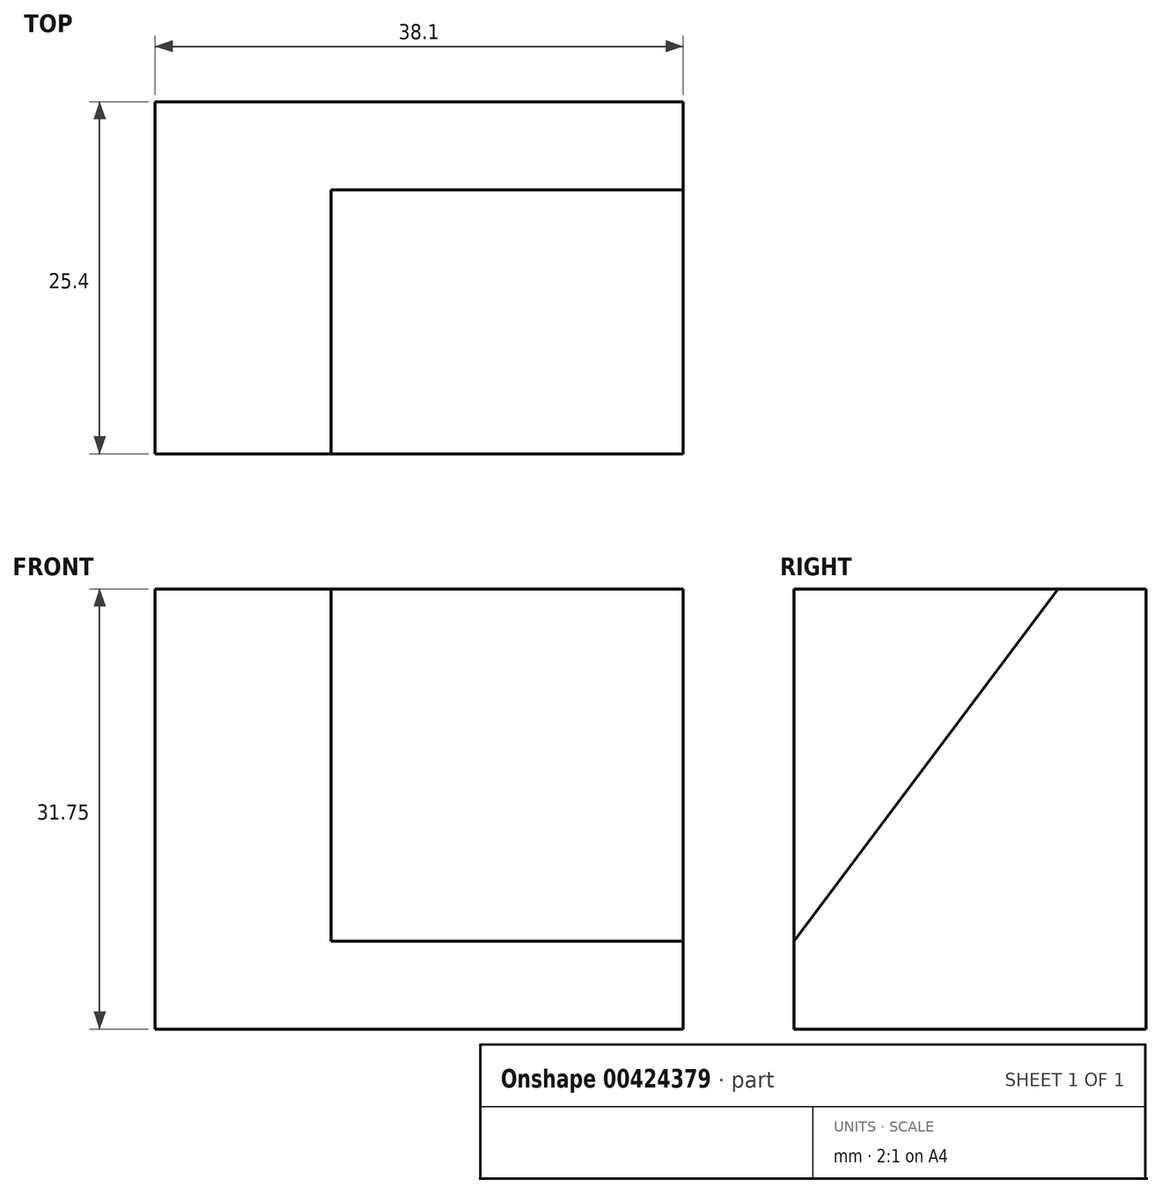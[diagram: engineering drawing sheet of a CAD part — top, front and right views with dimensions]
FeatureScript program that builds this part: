
annotation { "Feature Type Name" : "Feature", "Feature Type Description" : "" }
export const myFeature = defineFeature(function(context is Context, id is Id, definition is map)
    precondition{}
    {
        {
            var Q0;
            Q0=qCreatedBy(makeId("Top.planeOp"),FACE);
            var sketch = newSketch(context, id + "F0", { "sketchPlane" : qUnion([Q0])});
            skLineSegment(sketch, "E0", {"start": v(0, 0) * mm, "end": v(38.1, 0) * mm});
            skLineSegment(sketch, "E1", {"start": v(38.1, 0) * mm, "end": v(38.1, 25.4) * mm});
            skLineSegment(sketch, "E2", {"start": v(38.1, 25.4) * mm, "end": v(0, 25.4) * mm});
            skLineSegment(sketch, "E3", {"start": v(0, 25.4) * mm, "end": v(0, 0) * mm});
            skSolve(sketch);
        }
        {
            var Q0;
            Q0=makeQuery(id+"F0.imprint","IMPRINT",FACE,{"disambiguationData":[TD([[makeQuery(id+"F0.imprint","IMPRINT",EDGE,{"derivedFrom":sQuery(id+"F0.wireOp",EDGE,"E0")}),1.0]])]});
            extrude(context, id + "F1", {"entities" : qUnion([Q0]), "depth" : 31.75 * mm});
        }
        {
            var Q0;
            Q0=makeQuery(id+"F1.opExtrude","SWEPT_FACE",FACE,{"disambiguationData":[OSD([sQuery(id+"F0.wireOp",EDGE,"E1")])]});
            var sketch = newSketch(context, id + "F2", { "sketchPlane" : qUnion([Q0])});
            skLineSegment(sketch, "E4", {"start": v(25.4, 31.75) * mm, "end": v(19.05, 31.75) * mm});
            skLineSegment(sketch, "E5", {"start": v(0, 0) * mm, "end": v(0, 6.35) * mm});
            skLineSegment(sketch, "E6", {"start": v(19.05, 31.75) * mm, "end": v(0, 6.35) * mm});
            skSolve(sketch);
        }
        {
            var Q0;
            {var subQ0=sQuery(id+"F2.wireOp",EDGE,"E6");Q0=makeQuery(id+"F2.imprint","IMPRINT",FACE,{"disambiguationData":[TD([[makeQuery(id+"F2.imprint","IMPRINT",EDGE,{"derivedFrom":subQ0}),-1.0]])]});}
            extrude(context, id + "F3", {"entities" : qUnion([Q0]), "operationType" : NewBodyOperationType.REMOVE, "oppositeDirection" : true, "depth" : 25.4 * mm});
        }
    });
